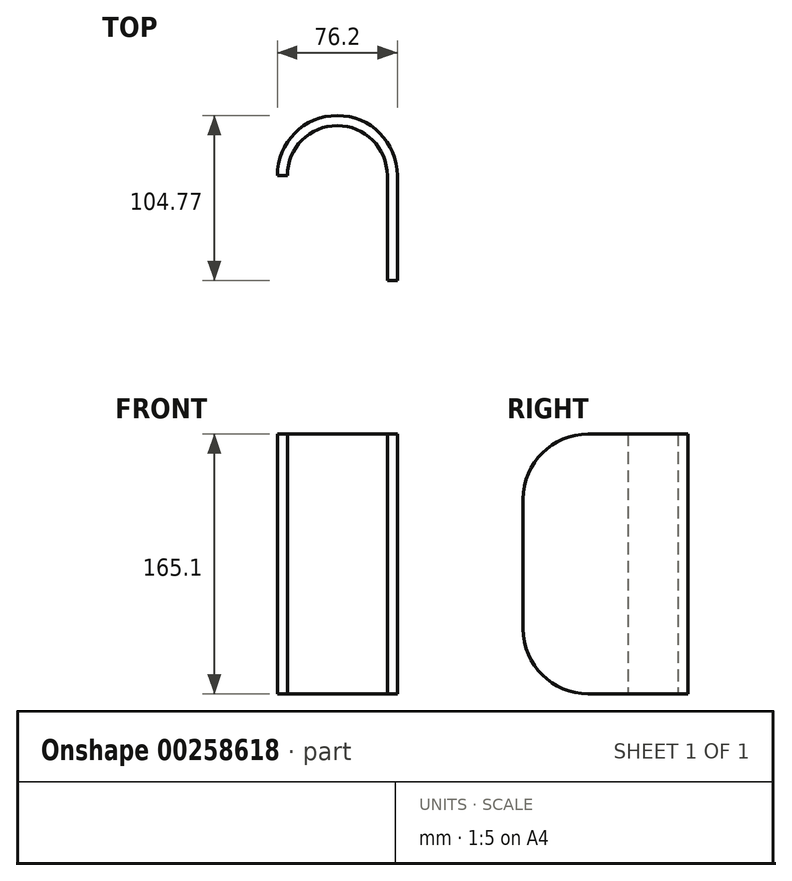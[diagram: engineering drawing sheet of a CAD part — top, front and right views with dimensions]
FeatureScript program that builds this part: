
annotation { "Feature Type Name" : "Feature", "Feature Type Description" : "" }
export const myFeature = defineFeature(function(context is Context, id is Id, definition is map)
    precondition{}
    {
        {
            var Q0;
            Q0=qCreatedBy(makeId("Top.planeOp"),FACE);
            var sketch = newSketch(context, id + "F0", { "sketchPlane" : qUnion([Q0])});
            skArc(sketch, "E0", {"start": v(38.1, 0) * mm, "mid": v(0, 38.1) * mm, "end": v(-38.1, 0) * mm});
            skArc(sketch, "E1", {"start": v(31.75, 0) * mm, "mid": v(0, 31.75) * mm, "end": v(-31.75, 0) * mm});
            skLineSegment(sketch, "E2", {"start": v(0, 0) * mm, "end": v(31.75, 0) * mm});
            skLineSegment(sketch, "E3", {"start": v(31.75, 0) * mm, "end": v(38.1, 0) * mm});
            skLineSegment(sketch, "E4", {"start": v(0, 0) * mm, "end": v(-38.1, 0) * mm});
            skLineSegment(sketch, "E5.bottom", {"start": v(-38.1, 0) * mm, "end": v(-31.75, 0) * mm});
            skLineSegment(sketch, "E5.top", {"start": v(-38.1, -66.68) * mm, "end": v(-31.75, -66.68) * mm});
            skLineSegment(sketch, "E5.left", {"start": v(-38.1, 0) * mm, "end": v(-38.1, -66.68) * mm});
            skLineSegment(sketch, "E5.right", {"start": v(-31.75, 0) * mm, "end": v(-31.75, -66.68) * mm});
            skLineSegment(sketch, "E6.top", {"start": v(31.75, -66.68) * mm, "end": v(38.1, -66.68) * mm});
            skLineSegment(sketch, "E6.left", {"start": v(31.75, 0) * mm, "end": v(31.75, -66.68) * mm});
            skLineSegment(sketch, "E6.right", {"start": v(38.1, 0) * mm, "end": v(38.1, -66.68) * mm});
            skSolve(sketch);
        }
        {
            var Q0;
            Q0=makeQuery(id+"F0.imprint","IMPRINT",FACE,{"disambiguationData":[TD([[makeQuery(id+"F0.imprint","IMPRINT",EDGE,{"derivedFrom":sQuery(id+"F0.wireOp",EDGE,"E0")}),1.0]])]});
            var Q1;
            Q1=makeQuery(id+"F0.imprint","IMPRINT",FACE,{"disambiguationData":[TD([[makeQuery(id+"F0.imprint","IMPRINT",EDGE,{"derivedFrom":sQuery(id+"F0.wireOp",EDGE,"E5.bottom")}),-1.0]])]});
            var Q2;
            Q2=makeQuery(id+"F0.imprint","IMPRINT",FACE,{"disambiguationData":[TD([[makeQuery(id+"F0.imprint","IMPRINT",EDGE,{"derivedFrom":sQuery(id+"F0.wireOp",EDGE,"E3")}),-1.0]])]});
            extrude(context, id + "F1", {"entities" : qUnion([Q0, Q1, Q2]), "depth" : 165.1 * mm});
        }
        {
            var Q0;
            Q0=makeQuery(id+"F1.opExtrude","CAP_EDGE",EDGE,{"disambiguationData":[OSD([sQuery(id+"F0.wireOp",EDGE,"E5.top")])],"isStart":false});
            var Q1;
            Q1=makeQuery(id+"F1.opExtrude","CAP_EDGE",EDGE,{"disambiguationData":[OSD([sQuery(id+"F0.wireOp",EDGE,"E6.top")])],"isStart":false});
            var Q2;
            Q2=makeQuery(id+"F1.opExtrude","CAP_EDGE",EDGE,{"disambiguationData":[OSD([sQuery(id+"F0.wireOp",EDGE,"E5.top")])],"isStart":true});
            var Q3;
            Q3=makeQuery(id+"F1.opExtrude","CAP_EDGE",EDGE,{"disambiguationData":[OSD([sQuery(id+"F0.wireOp",EDGE,"E6.top")])],"isStart":true});
            fillet(context, id + "F2", {"entities" : qUnion([Q0, Q1, Q2, Q3]), "radius" : 41.27 * mm, "tangentPropagation" : true, "allowEdgeOverflow" : false});
        }
    });
